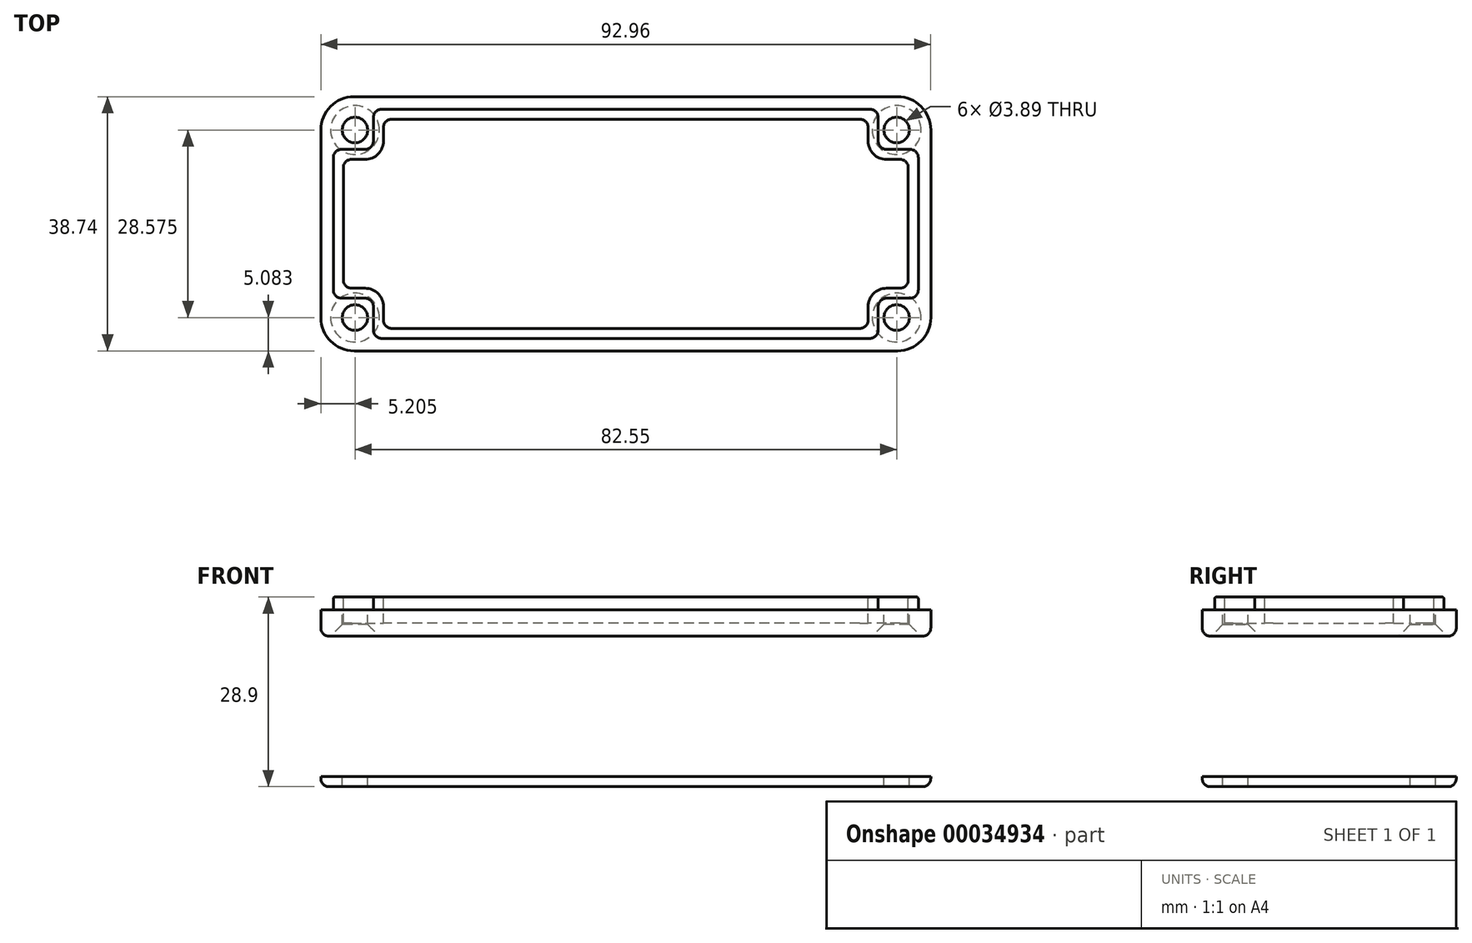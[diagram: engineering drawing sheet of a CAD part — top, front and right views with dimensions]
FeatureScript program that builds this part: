
annotation { "Feature Type Name" : "Feature", "Feature Type Description" : "" }
export const myFeature = defineFeature(function(context is Context, id is Id, definition is map)
    precondition{}
    {
        {
            var Q0;
            Q0=qCreatedBy(makeId("Top.planeOp"),FACE);
            var sketch = newSketch(context, id + "F0", { "sketchPlane" : qUnion([Q0])});
            skLineSegment(sketch, "E0.rect.bottom", {"start": v(41.4, 19.37) * mm, "end": v(-41.4, 19.37) * mm});
            skLineSegment(sketch, "E0.rect.top", {"start": v(41.4, -19.37) * mm, "end": v(-41.4, -19.37) * mm});
            skLineSegment(sketch, "E0.rect.left", {"start": v(46.48, 14.29) * mm, "end": v(46.48, -14.29) * mm});
            skLineSegment(sketch, "E0.rect.right", {"start": v(-46.48, 14.29) * mm, "end": v(-46.48, -14.29) * mm});
            skPoint(sketch, "E0.rect.middle", {"position": v(0, 0) * mm});
            skLineSegment(sketch, "E1.rect.bottom", {"start": v(37.19, -17.46) * mm, "end": v(-37.19, -17.46) * mm});
            skLineSegment(sketch, "E1.rect.top", {"start": v(37.19, 17.46) * mm, "end": v(-37.19, 17.46) * mm});
            skLineSegment(sketch, "E1.rect.left", {"start": v(44.58, -10.07) * mm, "end": v(44.58, 10.07) * mm});
            skLineSegment(sketch, "E1.rect.right", {"start": v(-44.58, -10.07) * mm, "end": v(-44.58, 10.07) * mm});
            skLineSegment(sketch, "E2.bottom", {"start": v(41.4, -19.37) * mm, "end": v(38.46, -19.37) * mm});
            skLineSegment(sketch, "E2.top", {"start": v(43.3, -11.34) * mm, "end": v(39.73, -11.34) * mm});
            skLineSegment(sketch, "E2.left", {"start": v(46.48, -14.29) * mm, "end": v(46.48, -11.34) * mm});
            skLineSegment(sketch, "E2.right", {"start": v(38.46, -16.2) * mm, "end": v(38.46, -12.61) * mm});
            skLineSegment(sketch, "E3.MirrorCS", {"start": v(-43.3, -11.34) * mm, "end": v(-39.73, -11.34) * mm});
            skLineSegment(sketch, "E4.MirrorCS", {"start": v(-38.46, -16.2) * mm, "end": v(-38.46, -12.61) * mm});
            skLineSegment(sketch, "E5.MirrorCS", {"start": v(-46.48, -14.29) * mm, "end": v(-46.48, -11.34) * mm});
            skLineSegment(sketch, "E6.MirrorCS", {"start": v(-41.4, -19.37) * mm, "end": v(-38.46, -19.37) * mm});
            skLineSegment(sketch, "E7.MirrorCS", {"start": v(43.3, 11.34) * mm, "end": v(39.73, 11.34) * mm});
            skLineSegment(sketch, "E8.MirrorCS", {"start": v(38.46, 16.2) * mm, "end": v(38.46, 12.61) * mm});
            skLineSegment(sketch, "E9.MirrorCS", {"start": v(41.4, 19.37) * mm, "end": v(38.46, 19.37) * mm});
            skLineSegment(sketch, "E10.MirrorCS", {"start": v(46.48, 14.29) * mm, "end": v(46.48, 11.34) * mm});
            skLineSegment(sketch, "E11.MirrorCS", {"start": v(-43.3, 11.34) * mm, "end": v(-39.73, 11.34) * mm});
            skLineSegment(sketch, "E12.MirrorCS", {"start": v(-38.46, 16.2) * mm, "end": v(-38.46, 12.61) * mm});
            skCircle(sketch, "E13", {"center": v(41.28, 14.29) * mm, "radius": 1.94 * mm});
            skCircle(sketch, "E14.MirrorC", {"center": v(-41.28, 14.29) * mm, "radius": 1.94 * mm});
            skCircle(sketch, "E15.MirrorC", {"center": v(-41.28, -14.29) * mm, "radius": 1.94 * mm});
            skCircle(sketch, "E16.MirrorC", {"center": v(41.28, -14.29) * mm, "radius": 1.94 * mm});
            skPoint(sketch, "E17.visualSharp", {"position": v(-46.48, 19.37) * mm});
            skArc(sketch, "E17.filletArc", {"start": v(-41.4, 19.37) * mm, "mid": v(-45, 17.88) * mm, "end": v(-46.48, 14.29) * mm});
            skPoint(sketch, "E18.visualSharp", {"position": v(46.48, 19.37) * mm});
            skArc(sketch, "E18.filletArc", {"start": v(46.48, 14.29) * mm, "mid": v(45, 17.88) * mm, "end": v(41.4, 19.37) * mm});
            skPoint(sketch, "E19.visualSharp", {"position": v(-46.48, -19.37) * mm});
            skArc(sketch, "E19.filletArc", {"start": v(-46.48, -14.29) * mm, "mid": v(-45, -17.88) * mm, "end": v(-41.4, -19.37) * mm});
            skPoint(sketch, "E20.visualSharp", {"position": v(46.48, -19.37) * mm});
            skArc(sketch, "E20.filletArc", {"start": v(41.4, -19.37) * mm, "mid": v(45, -17.88) * mm, "end": v(46.48, -14.29) * mm});
            skPoint(sketch, "E21.orphan", {"position": v(-44.58, 17.46) * mm});
            skPoint(sketch, "E22.orphan", {"position": v(-44.58, -17.46) * mm});
            skPoint(sketch, "E23.orphan", {"position": v(-38.46, 19.37) * mm});
            skPoint(sketch, "E24.orphan", {"position": v(-46.48, 11.34) * mm});
            skPoint(sketch, "E25.orphan", {"position": v(-46.48, -11.34) * mm});
            skPoint(sketch, "E26.orphan", {"position": v(-38.46, -19.37) * mm});
            skPoint(sketch, "E27.orphan", {"position": v(38.46, 19.37) * mm});
            skPoint(sketch, "E28.orphan", {"position": v(44.58, 17.46) * mm});
            skPoint(sketch, "E29.orphan", {"position": v(46.48, 11.34) * mm});
            skPoint(sketch, "E30.orphan", {"position": v(44.58, -17.46) * mm});
            skPoint(sketch, "E31.visualSharp", {"position": v(-38.46, 17.46) * mm});
            skArc(sketch, "E31.filletArc", {"start": v(-37.19, 17.46) * mm, "mid": v(-38.08, 17.1) * mm, "end": v(-38.46, 16.2) * mm});
            skPoint(sketch, "E32.visualSharp", {"position": v(-44.58, 11.34) * mm});
            skArc(sketch, "E32.filletArc", {"start": v(-43.3, 11.34) * mm, "mid": v(-44.2, 10.97) * mm, "end": v(-44.58, 10.07) * mm});
            skPoint(sketch, "E33.visualSharp", {"position": v(-44.58, -11.34) * mm});
            skArc(sketch, "E33.filletArc", {"start": v(-44.58, -10.07) * mm, "mid": v(-44.2, -10.97) * mm, "end": v(-43.3, -11.34) * mm});
            skPoint(sketch, "E34.visualSharp", {"position": v(-38.46, -17.46) * mm});
            skArc(sketch, "E34.filletArc", {"start": v(-38.46, -16.2) * mm, "mid": v(-38.08, -17.1) * mm, "end": v(-37.19, -17.46) * mm});
            skPoint(sketch, "E35.visualSharp", {"position": v(38.46, 17.46) * mm});
            skArc(sketch, "E35.filletArc", {"start": v(38.46, 16.2) * mm, "mid": v(38.08, 17.1) * mm, "end": v(37.19, 17.46) * mm});
            skPoint(sketch, "E36.visualSharp", {"position": v(44.58, 11.34) * mm});
            skArc(sketch, "E36.filletArc", {"start": v(44.58, 10.07) * mm, "mid": v(44.2, 10.97) * mm, "end": v(43.3, 11.34) * mm});
            skPoint(sketch, "E37.visualSharp", {"position": v(44.58, -11.34) * mm});
            skArc(sketch, "E37.filletArc", {"start": v(43.3, -11.34) * mm, "mid": v(44.2, -10.97) * mm, "end": v(44.58, -10.07) * mm});
            skPoint(sketch, "E38.visualSharp", {"position": v(38.46, -17.46) * mm});
            skArc(sketch, "E38.filletArc", {"start": v(37.19, -17.46) * mm, "mid": v(38.08, -17.1) * mm, "end": v(38.46, -16.2) * mm});
            skPoint(sketch, "E39.visualSharp", {"position": v(-38.46, 11.34) * mm});
            skArc(sketch, "E39.filletArc", {"start": v(-39.73, 11.34) * mm, "mid": v(-38.83, 11.71) * mm, "end": v(-38.46, 12.61) * mm});
            skPoint(sketch, "E40.visualSharp", {"position": v(-38.46, -11.34) * mm});
            skArc(sketch, "E40.filletArc", {"start": v(-38.46, -12.61) * mm, "mid": v(-38.83, -11.71) * mm, "end": v(-39.73, -11.34) * mm});
            skPoint(sketch, "E41.visualSharp", {"position": v(38.46, 11.34) * mm});
            skArc(sketch, "E41.filletArc", {"start": v(38.46, 12.61) * mm, "mid": v(38.83, 11.71) * mm, "end": v(39.73, 11.34) * mm});
            skPoint(sketch, "E42.visualSharp", {"position": v(38.46, -11.34) * mm});
            skArc(sketch, "E42.filletArc", {"start": v(39.73, -11.34) * mm, "mid": v(38.83, -11.71) * mm, "end": v(38.46, -12.61) * mm});
            skLineSegment(sketch, "E43.0", {"start": v(35.66, 15.94) * mm, "end": v(-35.66, 15.94) * mm});
            skLineSegment(sketch, "E44.0", {"start": v(35.66, -15.94) * mm, "end": v(-35.66, -15.94) * mm});
            skLineSegment(sketch, "E45.0", {"start": v(-43.05, -8.55) * mm, "end": v(-43.05, 8.55) * mm});
            skLineSegment(sketch, "E46.0", {"start": v(43.05, -8.55) * mm, "end": v(43.05, 8.55) * mm});
            skLineSegment(sketch, "E47.0", {"start": v(-36.93, 14.67) * mm, "end": v(-36.93, 12.61) * mm});
            skLineSegment(sketch, "E48.0", {"start": v(-41.78, 9.82) * mm, "end": v(-39.73, 9.82) * mm});
            skLineSegment(sketch, "E49.0", {"start": v(-41.78, -9.82) * mm, "end": v(-39.73, -9.82) * mm});
            skLineSegment(sketch, "E50.0", {"start": v(-36.93, -14.67) * mm, "end": v(-36.93, -12.61) * mm});
            skLineSegment(sketch, "E51.0", {"start": v(36.93, 14.67) * mm, "end": v(36.93, 12.61) * mm});
            skLineSegment(sketch, "E52.0", {"start": v(41.78, 9.82) * mm, "end": v(39.73, 9.82) * mm});
            skLineSegment(sketch, "E53.0", {"start": v(41.78, -9.82) * mm, "end": v(39.73, -9.82) * mm});
            skLineSegment(sketch, "E54.0", {"start": v(36.93, -14.67) * mm, "end": v(36.93, -12.61) * mm});
            skArc(sketch, "E55", {"start": v(-39.73, 9.82) * mm, "mid": v(-37.75, 10.64) * mm, "end": v(-36.93, 12.61) * mm});
            skPoint(sketch, "E56.visualSharp", {"position": v(-36.93, 15.94) * mm});
            skArc(sketch, "E56.filletArc", {"start": v(-35.66, 15.94) * mm, "mid": v(-36.56, 15.57) * mm, "end": v(-36.93, 14.67) * mm});
            skPoint(sketch, "E57.visualSharp", {"position": v(-43.05, 9.82) * mm});
            skArc(sketch, "E57.filletArc", {"start": v(-41.78, 9.82) * mm, "mid": v(-42.68, 9.45) * mm, "end": v(-43.05, 8.55) * mm});
            skArc(sketch, "E58", {"start": v(-36.93, -12.61) * mm, "mid": v(-37.75, -10.64) * mm, "end": v(-39.73, -9.82) * mm});
            skPoint(sketch, "E59.visualSharp", {"position": v(-43.05, -9.82) * mm});
            skArc(sketch, "E59.filletArc", {"start": v(-43.05, -8.55) * mm, "mid": v(-42.68, -9.45) * mm, "end": v(-41.78, -9.82) * mm});
            skPoint(sketch, "E60.visualSharp", {"position": v(-36.93, -15.94) * mm});
            skArc(sketch, "E60.filletArc", {"start": v(-36.93, -14.67) * mm, "mid": v(-36.56, -15.57) * mm, "end": v(-35.66, -15.94) * mm});
            skArc(sketch, "E61", {"start": v(36.93, 12.61) * mm, "mid": v(37.75, 10.64) * mm, "end": v(39.73, 9.82) * mm});
            skPoint(sketch, "E62.visualSharp", {"position": v(36.93, 15.94) * mm});
            skArc(sketch, "E62.filletArc", {"start": v(36.93, 14.67) * mm, "mid": v(36.56, 15.57) * mm, "end": v(35.66, 15.94) * mm});
            skPoint(sketch, "E63.visualSharp", {"position": v(43.05, 9.82) * mm});
            skArc(sketch, "E63.filletArc", {"start": v(43.05, 8.55) * mm, "mid": v(42.68, 9.45) * mm, "end": v(41.78, 9.82) * mm});
            skArc(sketch, "E64", {"start": v(39.73, -9.82) * mm, "mid": v(37.75, -10.64) * mm, "end": v(36.93, -12.61) * mm});
            skPoint(sketch, "E65.visualSharp", {"position": v(43.05, -9.82) * mm});
            skArc(sketch, "E65.filletArc", {"start": v(41.78, -9.82) * mm, "mid": v(42.68, -9.45) * mm, "end": v(43.05, -8.55) * mm});
            skPoint(sketch, "E66.visualSharp", {"position": v(36.93, -15.94) * mm});
            skArc(sketch, "E66.filletArc", {"start": v(35.66, -15.94) * mm, "mid": v(36.56, -15.57) * mm, "end": v(36.93, -14.67) * mm});
            skSolve(sketch);
        }
        {
            var Q0;
            Q0 = qSketchRegion(id + "F0", true);
            var Q1;
            Q1=makeQuery(id+"F0.imprint","IMPRINT",FACE,{"disambiguationData":[TD([[makeQuery(id+"F0.imprint","IMPRINT",EDGE,{"derivedFrom":sQuery(id+"F0.wireOp",EDGE,"E1.rect.bottom")}),-1.0]])]});
            var Q2;
            Q2=makeQuery(id+"F0.imprint","IMPRINT",FACE,{"disambiguationData":[TD([[makeQuery(id+"F0.imprint","IMPRINT",EDGE,{"derivedFrom":sQuery(id+"F0.wireOp",EDGE,"E13")}),1.0]])]});
            var Q3;
            Q3=makeQuery(id+"F0.imprint","IMPRINT",FACE,{"disambiguationData":[TD([[makeQuery(id+"F0.imprint","IMPRINT",EDGE,{"derivedFrom":sQuery(id+"F0.wireOp",EDGE,"E16.MirrorC")}),-1.0]])]});
            var Q4;
            Q4=makeQuery(id+"F0.imprint","IMPRINT",FACE,{"disambiguationData":[TD([[makeQuery(id+"F0.imprint","IMPRINT",EDGE,{"derivedFrom":sQuery(id+"F0.wireOp",EDGE,"E15.MirrorC")}),1.0]])]});
            var Q5;
            Q5=makeQuery(id+"F0.imprint","IMPRINT",FACE,{"disambiguationData":[TD([[makeQuery(id+"F0.imprint","IMPRINT",EDGE,{"derivedFrom":sQuery(id+"F0.wireOp",EDGE,"E14.MirrorC")}),-1.0]])]});
            var Q6;
            Q6=makeQuery(id+"F0.imprint","IMPRINT",FACE,{"disambiguationData":[TD([[makeQuery(id+"F0.imprint","IMPRINT",EDGE,{"derivedFrom":sQuery(id+"F0.wireOp",EDGE,"E43.0")}),1.0]])]});
            extrude(context, id + "F1", {"entities" : qUnion([Q0, Q1, Q2, Q3, Q4, Q5, Q6]), "oppositeDirection" : true, "depth" : 26.92 * mm});
        }
        {
            var Q0;
            Q0=makeQuery(id+"F0.imprint","IMPRINT",FACE,{"disambiguationData":[TD([[makeQuery(id+"F0.imprint","IMPRINT",EDGE,{"derivedFrom":sQuery(id+"F0.wireOp",EDGE,"E14.MirrorC")}),-1.0]])]});
            var Q1;
            Q1=makeQuery(id+"F0.imprint","IMPRINT",FACE,{"disambiguationData":[TD([[makeQuery(id+"F0.imprint","IMPRINT",EDGE,{"derivedFrom":sQuery(id+"F0.wireOp",EDGE,"E15.MirrorC")}),1.0]])]});
            var Q2;
            Q2=makeQuery(id+"F0.imprint","IMPRINT",FACE,{"disambiguationData":[TD([[makeQuery(id+"F0.imprint","IMPRINT",EDGE,{"derivedFrom":sQuery(id+"F0.wireOp",EDGE,"E1.rect.bottom")}),-1.0]])]});
            var Q3;
            Q3=makeQuery(id+"F0.imprint","IMPRINT",FACE,{"disambiguationData":[TD([[makeQuery(id+"F0.imprint","IMPRINT",EDGE,{"derivedFrom":sQuery(id+"F0.wireOp",EDGE,"E13")}),1.0]])]});
            var Q4;
            Q4=makeQuery(id+"F0.imprint","IMPRINT",FACE,{"disambiguationData":[TD([[makeQuery(id+"F0.imprint","IMPRINT",EDGE,{"derivedFrom":sQuery(id+"F0.wireOp",EDGE,"E16.MirrorC")}),-1.0]])]});
            var Q5;
            Q5=makeQuery(id+"F0.imprint","IMPRINT",FACE,{"disambiguationData":[TD([[makeQuery(id+"F0.imprint","IMPRINT",EDGE,{"derivedFrom":sQuery(id+"F0.wireOp",EDGE,"E43.0")}),1.0]])]});
            extrude(context, id + "F2", {"entities" : qUnion([Q0, Q1, Q2, Q3, Q4, Q5]), "operationType" : NewBodyOperationType.REMOVE, "oppositeDirection" : true, "depth" : 25.4 * mm});
        }
        {
            var Q0;
            Q0 = qSketchRegion(id + "F0", true);
            var Q1;
            Q1=makeQuery(id+"F0.imprint","IMPRINT",FACE,{"disambiguationData":[TD([[makeQuery(id+"F0.imprint","IMPRINT",EDGE,{"derivedFrom":sQuery(id+"F0.wireOp",EDGE,"E1.rect.bottom")}),-1.0]])]});
            var Q2;
            Q2=makeQuery(id+"F0.imprint","IMPRINT",FACE,{"disambiguationData":[TD([[makeQuery(id+"F0.imprint","IMPRINT",EDGE,{"derivedFrom":sQuery(id+"F0.wireOp",EDGE,"E43.0")}),1.0]])]});
            extrude(context, id + "F3", {"entities" : qUnion([Q0, Q1, Q2]), "oppositeDirection" : true, "depth" : 4 * mm});
        }
        {
            var Q0;
            Q0=makeQuery(id+"F0.imprint","IMPRINT",FACE,{"disambiguationData":[TD([[makeQuery(id+"F0.imprint","IMPRINT",EDGE,{"derivedFrom":sQuery(id+"F0.wireOp",EDGE,"E43.0")}),1.0]])]});
            extrude(context, id + "F4", {"entities" : qUnion([Q0]), "operationType" : NewBodyOperationType.REMOVE, "oppositeDirection" : true, "depth" : 2.03 * mm});
        }
        {
            var Q0;
            Q0=makeQuery(id+"F0.imprint","IMPRINT",FACE,{"disambiguationData":[TD([[makeQuery(id+"F0.imprint","IMPRINT",EDGE,{"derivedFrom":sQuery(id+"F0.wireOp",EDGE,"E1.rect.bottom")}),-1.0]])]});
            extrude(context, id + "F5", {"entities" : qUnion([Q0]), "operationType" : NewBodyOperationType.ADD, "depth" : 1.98 * mm});
        }
        {
            var Q0;
            Q0=makeQuery(id+"F3.opExtrude","CAP_EDGE",EDGE,{"disambiguationData":[OSD([sQuery(id+"F0.wireOp",EDGE,"E0.rect.right"),sQuery(id+"F0.wireOp",EDGE,"E5.MirrorCS")])],"isStart":false});
            fillet(context, id + "F6", {"entities" : qUnion([Q0]), "radius" : 1.27 * mm, "tangentPropagation" : true, "allowEdgeOverflow" : false});
        }
        {
            var Q0;
            Q0=makeQuery(id+"F3.opExtrude","CAP_EDGE",EDGE,{"disambiguationData":[OSD([sQuery(id+"F0.wireOp",EDGE,"E14.MirrorC")])],"isStart":false});
            chamfer(context, id + "F7", {"entities" : qUnion([Q0]), "width" : 1.78 * mm, "tangentPropagation" : true});
        }
        {
            var Q0;
            Q0=makeQuery(id+"F3.opExtrude","CAP_EDGE",EDGE,{"disambiguationData":[OSD([sQuery(id+"F0.wireOp",EDGE,"E15.MirrorC")])],"isStart":false});
            var Q1;
            Q1=makeQuery(id+"F3.opExtrude","CAP_EDGE",EDGE,{"disambiguationData":[OSD([sQuery(id+"F0.wireOp",EDGE,"E13")])],"isStart":false});
            var Q2;
            Q2=makeQuery(id+"F3.opExtrude","CAP_EDGE",EDGE,{"disambiguationData":[OSD([sQuery(id+"F0.wireOp",EDGE,"E16.MirrorC")])],"isStart":false});
            chamfer(context, id + "F8", {"entities" : qUnion([Q0, Q1, Q2]), "width" : 1.78 * mm, "tangentPropagation" : true});
        }
        {
            var Q0;
            Q0=makeQuery(id+"F5.opExtrude","CAP_EDGE",EDGE,{"disambiguationData":[OSD([sQuery(id+"F0.wireOp",EDGE,"E1.rect.bottom")])],"isStart":false});
            var Q1;
            Q1=makeQuery(id+"F5.opExtrude","CAP_EDGE",EDGE,{"disambiguationData":[OSD([sQuery(id+"F0.wireOp",EDGE,"E43.0")])],"isStart":false});
            fillet(context, id + "F9", {"entities" : qUnion([Q0, Q1]), "radius" : 0.25 * mm, "tangentPropagation" : true, "allowEdgeOverflow" : false});
        }
        {
            var Q0;
            Q0=makeQuery(id+"F1.opExtrude","CAP_EDGE",EDGE,{"disambiguationData":[OSD([sQuery(id+"F0.wireOp",EDGE,"E0.rect.bottom"),sQuery(id+"F0.wireOp",EDGE,"E9.MirrorCS")])],"isStart":false});
            fillet(context, id + "F10", {"entities" : qUnion([Q0]), "radius" : 1.27 * mm, "tangentPropagation" : true, "allowEdgeOverflow" : false});
        }
    });
